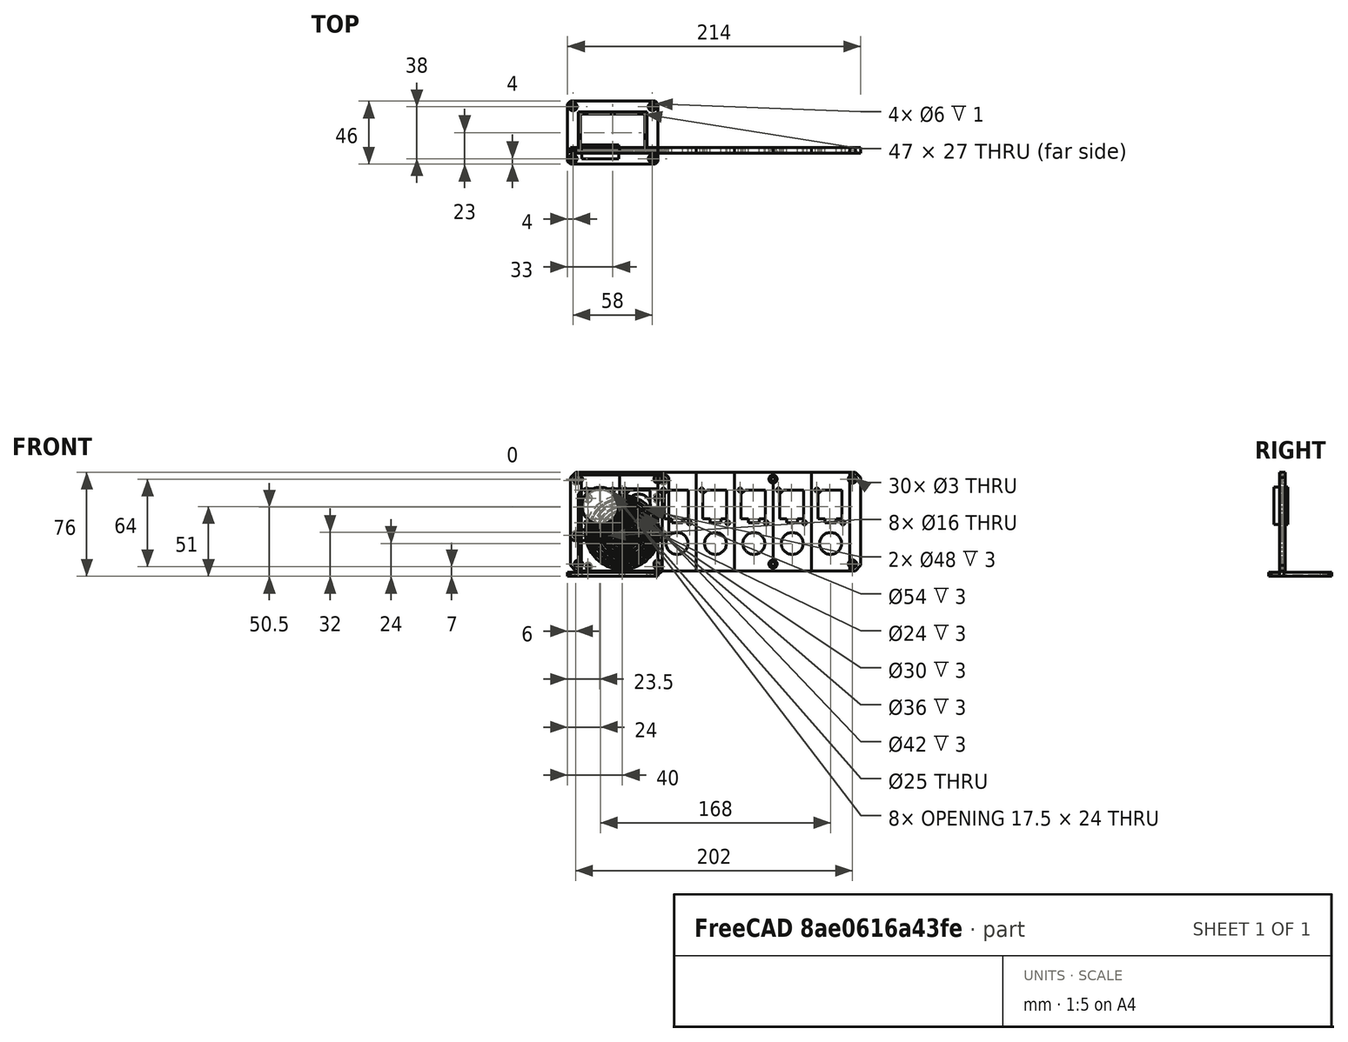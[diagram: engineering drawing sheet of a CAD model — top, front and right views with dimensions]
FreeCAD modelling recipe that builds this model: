
FCSTD DOCUMENT  (FreeCAD 0.19R24276 (Git))
Label: gewisska_016
License: All rights reserved
LicenseURL: http://en.wikipedia.org/wiki/All_rights_reserved
objects: Part::Cylinder×72, Part::Box×36, Part::Compound×34, Part::Cut×26, Part::Chamfer×16, Part::FeaturePython×9, Mesh::Feature×4
note: 193 computed .brp shape members not serialized (recipe doc carries the construction recipe); baked Part::Feature solids carry a one-line shape summary decoded from their .brp

FEATURE [Part::Box] Box  label="Krychle"
  AttacherType = Attacher::AttachEngine3D
  Height = 3
  Length = 50
  Placement = pos=(0,0,0.8) rot=(0,0,1;0rad)
  Width = 30
FEATURE [Part::Box] Box001  label="Krychle001"
  AttacherType = Attacher::AttachEngine3D
  Height = 3
  Length = 66
  Placement = pos=(-8,-8,0) rot=(0,0,1;0rad)
  Width = 46
FEATURE [Part::Box] Box002  label="Krychle002"
  AttacherType = Attacher::AttachEngine3D
  Height = 6
  Length = 47
  Placement = pos=(1.5,1.5,-1) rot=(0,0,1;0rad)
  Width = 27
FEATURE [Part::Cut] Cut
  Base = -> Box001
  Tool = -> Box002
FEATURE [Part::Cut] Cut001
  Base = -> Cut
  Tool = -> Box
FEATURE [Part::Cylinder] Cylinder  label="Válec"
  Angle = 360
  AttacherType = Attacher::AttachEngine3D
  Height = 10
  Placement = pos=(-4,34,-2) rot=(0,0,1;0rad)
  Radius = 1.5
FEATURE [Part::Cylinder] Cylinder001  label="Válec001"
  Angle = 360
  AttacherType = Attacher::AttachEngine3D
  Height = 10
  Placement = pos=(54,-4,-2) rot=(0,0,1;0rad)
  Radius = 1.5
FEATURE [Part::Cylinder] Cylinder002  label="Válec002"
  Angle = 360
  AttacherType = Attacher::AttachEngine3D
  Height = 10
  Placement = pos=(54,34,-2) rot=(0,0,1;0rad)
  Radius = 1.5
FEATURE [Part::Cylinder] Cylinder003  label="Válec003"
  Angle = 360
  AttacherType = Attacher::AttachEngine3D
  Height = 10
  Placement = pos=(-4,-4,-2) rot=(0,0,1;0rad)
  Radius = 1.5
FEATURE [Part::Compound] Compound
  Links = -> [Cylinder,Cylinder001,Cylinder002,Cylinder003]
FEATURE [Part::Cylinder] Cylinder004  label="Válec004"
  Angle = 360
  AttacherType = Attacher::AttachEngine3D
  Height = 3
  Placement = pos=(-4,-4,-2) rot=(0,0,1;0rad)
  Radius = 3
FEATURE [Part::Cylinder] Cylinder005  label="Válec005"
  Angle = 360
  AttacherType = Attacher::AttachEngine3D
  Height = 3
  Placement = pos=(-4,34,-2) rot=(0,0,1;0rad)
  Radius = 3
FEATURE [Part::Cylinder] Cylinder006  label="Válec006"
  Angle = 360
  AttacherType = Attacher::AttachEngine3D
  Height = 3
  Placement = pos=(54,34,-2) rot=(0,0,1;0rad)
  Radius = 3
FEATURE [Part::Cylinder] Cylinder007  label="Válec007"
  Angle = 360
  AttacherType = Attacher::AttachEngine3D
  Height = 3
  Placement = pos=(54,-4,-2) rot=(0,0,1;0rad)
  Radius = 3
FEATURE [Part::Compound] Compound001
  Links = -> [Cylinder005,Cylinder007,Cylinder006,Cylinder004]
  Placement = pos=(0,0,4) rot=(0,0,1;0rad)
FEATURE [Part::Cut] Cut002
  Base = -> Cut001
  Tool = -> Compound
FEATURE [Part::Cut] Cut003
  Base = -> Cut002
  Tool = -> Compound001
FEATURE [Part::Chamfer] Chamfer
  Base = -> Cut003
  Edges = 2 edges r=2: [Edge1,Edge6]
FEATURE [Part::Chamfer] Chamfer001  label="220_zasuvka_drzho"
  Base = -> Chamfer
  Edges = 2 edges r=2: [Edge4,Edge21]
FEATURE [Mesh::Feature] Mesh  label="220_zasuvka_drzho (Meshed)"
FEATURE [Part::Cylinder] Cylinder816  label="Válec816"
  Angle = 360
  AttacherType = Attacher::AttachEngine3D
  Height = 10
  Placement = pos=(29,6,39) rot=(1,0,0;1.5708rad)
  Radius = 1.5
FEATURE [Part::Cylinder] Cylinder815  label="Válec815"
  Angle = 360
  AttacherType = Attacher::AttachEngine3D
  Height = 10
  Placement = pos=(10,6,63) rot=(1,0,0;1.5708rad)
  Radius = 1.5
FEATURE [Part::Compound] Compound477
  Links = -> [Cylinder815,Cylinder816]
  Placement = pos=(-4,0,0) rot=(0,0,1;0rad)
FEATURE [Part::Box] Box390  label="Krychle390"
  AttacherType = Attacher::AttachEngine3D
  Height = 21
  Length = 17.5
  Placement = pos=(10.75,-2,42) rot=(0,0,1;0rad)
  Width = 10
FEATURE [Part::Chamfer] Chamfer014
  Base = -> Box390
  Edges = 1 edges r=3: [Edge2]
  Placement = pos=(-4,0,0) rot=(0,0,1;0rad)
FEATURE [Part::Cylinder] Cylinder828  label="Válec828"
  Angle = 360
  AttacherType = Attacher::AttachEngine3D
  Height = 10
  Placement = pos=(16,6,24) rot=(1,0,0;1.5708rad)
  Radius = 8
FEATURE [Part::Box] Box396  label="Krychle396"
  AttacherType = Attacher::AttachEngine3D
  Height = 3
  Length = 8
  Placement = pos=(12,-2,39) rot=(0,0,1;0rad)
  Width = 10
FEATURE [Part::Compound] Compound478
  Links = -> [Compound477,Chamfer014,Cylinder828,Box396]
FEATURE [Part::Box] Box397  label="Krychle397"
  AttacherType = Attacher::AttachEngine3D
  Height = 72
  Length = 28
  Placement = pos=(2,0,4) rot=(0,0,1;0rad)
  Width = 4
FEATURE [Part::Cut] Cut004
  Base = -> Box397
  Tool = -> Compound478
FEATURE [Part::Box] Box398  label="Krychle398"
  AttacherType = Attacher::AttachEngine3D
  Height = 72
  Length = 28
  Placement = pos=(2,0,4) rot=(0,0,1;0rad)
  Width = 4
FEATURE [Part::Box] Box399  label="Krychle399"
  AttacherType = Attacher::AttachEngine3D
  Height = 21
  Length = 17.5
  Placement = pos=(10.75,-2,42) rot=(0,0,1;0rad)
  Width = 10
FEATURE [Part::Cylinder] Cylinder829  label="Válec829"
  Angle = 360
  AttacherType = Attacher::AttachEngine3D
  Height = 10
  Placement = pos=(16,6,24) rot=(1,0,0;1.5708rad)
  Radius = 8
FEATURE [Part::Cylinder] Cylinder830  label="Válec830"
  Angle = 360
  AttacherType = Attacher::AttachEngine3D
  Height = 10
  Placement = pos=(29,6,39) rot=(1,0,0;1.5708rad)
  Radius = 1.5
FEATURE [Part::Cylinder] Cylinder831  label="Válec831"
  Angle = 360
  AttacherType = Attacher::AttachEngine3D
  Height = 10
  Placement = pos=(10,6,63) rot=(1,0,0;1.5708rad)
  Radius = 1.5
FEATURE [Part::Box] Box400  label="Krychle400"
  AttacherType = Attacher::AttachEngine3D
  Height = 3
  Length = 8
  Placement = pos=(12,-2,39) rot=(0,0,1;0rad)
  Width = 10
FEATURE [Part::Chamfer] Chamfer015
  Base = -> Box399
  Edges = 1 edges r=3: [Edge2]
  Placement = pos=(-4,0,0) rot=(0,0,1;0rad)
FEATURE [Part::Compound] Compound480
  Links = -> [Cylinder831,Cylinder830]
  Placement = pos=(-4,0,0) rot=(0,0,1;0rad)
FEATURE [Part::Compound] Compound479
  Links = -> [Compound480,Chamfer015,Cylinder829,Box400]
FEATURE [Part::Cut] Cut005
  Base = -> Box398
  Placement = pos=(28,0,0) rot=(0,0,1;0rad)
  Tool = -> Compound479
FEATURE [Part::Box] Box401  label="Krychle401"
  AttacherType = Attacher::AttachEngine3D
  Height = 72
  Length = 28
  Placement = pos=(2,0,4) rot=(0,0,1;0rad)
  Width = 4
FEATURE [Part::Box] Box402  label="Krychle402"
  AttacherType = Attacher::AttachEngine3D
  Height = 21
  Length = 17.5
  Placement = pos=(10.75,-2,42) rot=(0,0,1;0rad)
  Width = 10
FEATURE [Part::Cylinder] Cylinder832  label="Válec832"
  Angle = 360
  AttacherType = Attacher::AttachEngine3D
  Height = 10
  Placement = pos=(16,6,24) rot=(1,0,0;1.5708rad)
  Radius = 8
FEATURE [Part::Cylinder] Cylinder833  label="Válec833"
  Angle = 360
  AttacherType = Attacher::AttachEngine3D
  Height = 10
  Placement = pos=(29,6,39) rot=(1,0,0;1.5708rad)
  Radius = 1.5
FEATURE [Part::Cylinder] Cylinder834  label="Válec834"
  Angle = 360
  AttacherType = Attacher::AttachEngine3D
  Height = 10
  Placement = pos=(10,6,63) rot=(1,0,0;1.5708rad)
  Radius = 1.5
FEATURE [Part::Box] Box403  label="Krychle403"
  AttacherType = Attacher::AttachEngine3D
  Height = 3
  Length = 8
  Placement = pos=(12,-2,39) rot=(0,0,1;0rad)
  Width = 10
FEATURE [Part::Chamfer] Chamfer016
  Base = -> Box402
  Edges = 1 edges r=3: [Edge2]
  Placement = pos=(-4,0,0) rot=(0,0,1;0rad)
FEATURE [Part::Compound] Compound482
  Links = -> [Cylinder834,Cylinder833]
  Placement = pos=(-4,0,0) rot=(0,0,1;0rad)
FEATURE [Part::Compound] Compound481
  Links = -> [Compound482,Chamfer016,Cylinder832,Box403]
FEATURE [Part::Cut] Cut006
  Base = -> Box401
  Placement = pos=(56,0,0) rot=(0,0,1;0rad)
  Tool = -> Compound481
FEATURE [Part::Box] Box404  label="Krychle404"
  AttacherType = Attacher::AttachEngine3D
  Height = 72
  Length = 28
  Placement = pos=(2,0,4) rot=(0,0,1;0rad)
  Width = 4
FEATURE [Part::Box] Box405  label="Krychle405"
  AttacherType = Attacher::AttachEngine3D
  Height = 21
  Length = 17.5
  Placement = pos=(10.75,-2,42) rot=(0,0,1;0rad)
  Width = 10
FEATURE [Part::Cylinder] Cylinder835  label="Válec835"
  Angle = 360
  AttacherType = Attacher::AttachEngine3D
  Height = 10
  Placement = pos=(16,6,24) rot=(1,0,0;1.5708rad)
  Radius = 8
FEATURE [Part::Cylinder] Cylinder836  label="Válec836"
  Angle = 360
  AttacherType = Attacher::AttachEngine3D
  Height = 10
  Placement = pos=(29,6,39) rot=(1,0,0;1.5708rad)
  Radius = 1.5
FEATURE [Part::Cylinder] Cylinder837  label="Válec837"
  Angle = 360
  AttacherType = Attacher::AttachEngine3D
  Height = 10
  Placement = pos=(10,6,63) rot=(1,0,0;1.5708rad)
  Radius = 1.5
FEATURE [Part::Box] Box406  label="Krychle406"
  AttacherType = Attacher::AttachEngine3D
  Height = 3
  Length = 8
  Placement = pos=(12,-2,39) rot=(0,0,1;0rad)
  Width = 10
FEATURE [Part::Chamfer] Chamfer017
  Base = -> Box405
  Edges = 1 edges r=3: [Edge2]
  Placement = pos=(-4,0,0) rot=(0,0,1;0rad)
FEATURE [Part::Compound] Compound484
  Links = -> [Cylinder837,Cylinder836]
  Placement = pos=(-4,0,0) rot=(0,0,1;0rad)
FEATURE [Part::Compound] Compound483
  Links = -> [Compound484,Chamfer017,Cylinder835,Box406]
FEATURE [Part::Cut] Cut007
  Base = -> Box404
  Placement = pos=(84,0,0) rot=(0,0,1;0rad)
  Tool = -> Compound483
FEATURE [Part::Box] Box407  label="Krychle407"
  AttacherType = Attacher::AttachEngine3D
  Height = 3
  Length = 8
  Placement = pos=(12,-2,39) rot=(0,0,1;0rad)
  Width = 10
FEATURE [Part::Cylinder] Cylinder838  label="Válec838"
  Angle = 360
  AttacherType = Attacher::AttachEngine3D
  Height = 10
  Placement = pos=(10,6,63) rot=(1,0,0;1.5708rad)
  Radius = 1.5
FEATURE [Part::Cylinder] Cylinder839  label="Válec839"
  Angle = 360
  AttacherType = Attacher::AttachEngine3D
  Height = 10
  Placement = pos=(16,6,24) rot=(1,0,0;1.5708rad)
  Radius = 8
FEATURE [Part::Box] Box408  label="Krychle408"
  AttacherType = Attacher::AttachEngine3D
  Height = 21
  Length = 17.5
  Placement = pos=(10.75,-2,42) rot=(0,0,1;0rad)
  Width = 10
FEATURE [Part::Chamfer] Chamfer018
  Base = -> Box408
  Edges = 1 edges r=3: [Edge2]
  Placement = pos=(-4,0,0) rot=(0,0,1;0rad)
FEATURE [Part::Box] Box409  label="Krychle409"
  AttacherType = Attacher::AttachEngine3D
  Height = 72
  Length = 28
  Placement = pos=(2,0,4) rot=(0,0,1;0rad)
  Width = 4
FEATURE [Part::Cylinder] Cylinder840  label="Válec840"
  Angle = 360
  AttacherType = Attacher::AttachEngine3D
  Height = 10
  Placement = pos=(29,6,39) rot=(1,0,0;1.5708rad)
  Radius = 1.5
FEATURE [Part::Compound] Compound485
  Links = -> [Cylinder838,Cylinder840]
  Placement = pos=(-4,0,0) rot=(0,0,1;0rad)
FEATURE [Part::Compound] Compound486
  Links = -> [Compound485,Chamfer018,Cylinder839,Box407]
FEATURE [Part::Cut] Cut008
  Base = -> Box409
  Placement = pos=(112,0,0) rot=(0,0,1;0rad)
  Tool = -> Compound486
FEATURE [Part::Cylinder] Cylinder841  label="Válec841"
  Angle = 360
  AttacherType = Attacher::AttachEngine3D
  Height = 10
  Placement = pos=(10,6,63) rot=(1,0,0;1.5708rad)
  Radius = 1.5
FEATURE [Part::Box] Box410  label="Krychle410"
  AttacherType = Attacher::AttachEngine3D
  Height = 3
  Length = 8
  Placement = pos=(12,-2,39) rot=(0,0,1;0rad)
  Width = 10
FEATURE [Part::Cylinder] Cylinder842  label="Válec842"
  Angle = 360
  AttacherType = Attacher::AttachEngine3D
  Height = 10
  Placement = pos=(16,6,24) rot=(1,0,0;1.5708rad)
  Radius = 8
FEATURE [Part::Box] Box411  label="Krychle411"
  AttacherType = Attacher::AttachEngine3D
  Height = 21
  Length = 17.5
  Placement = pos=(10.75,-2,42) rot=(0,0,1;0rad)
  Width = 10
FEATURE [Part::Chamfer] Chamfer019
  Base = -> Box411
  Edges = 1 edges r=3: [Edge2]
  Placement = pos=(-4,0,0) rot=(0,0,1;0rad)
FEATURE [Part::Cylinder] Cylinder843  label="Válec843"
  Angle = 360
  AttacherType = Attacher::AttachEngine3D
  Height = 10
  Placement = pos=(29,6,39) rot=(1,0,0;1.5708rad)
  Radius = 1.5
FEATURE [Part::Compound] Compound487
  Links = -> [Cylinder841,Cylinder843]
  Placement = pos=(-4,0,0) rot=(0,0,1;0rad)
FEATURE [Part::Compound] Compound488
  Links = -> [Compound487,Chamfer019,Cylinder842,Box410]
FEATURE [Part::Box] Box412  label="Krychle412"
  AttacherType = Attacher::AttachEngine3D
  Height = 72
  Length = 28
  Placement = pos=(2,0,4) rot=(0,0,1;0rad)
  Width = 4
FEATURE [Part::Cut] Cut009
  Base = -> Box412
  Placement = pos=(140,0,0) rot=(0,0,1;0rad)
  Tool = -> Compound488
FEATURE [Part::Cylinder] Cylinder844  label="Válec844"
  Angle = 360
  AttacherType = Attacher::AttachEngine3D
  Height = 10
  Placement = pos=(10,6,63) rot=(1,0,0;1.5708rad)
  Radius = 1.5
FEATURE [Part::Box] Box413  label="Krychle413"
  AttacherType = Attacher::AttachEngine3D
  Height = 3
  Length = 8
  Placement = pos=(12,-2,39) rot=(0,0,1;0rad)
  Width = 10
FEATURE [Part::Cylinder] Cylinder845  label="Válec845"
  Angle = 360
  AttacherType = Attacher::AttachEngine3D
  Height = 10
  Placement = pos=(16,6,24) rot=(1,0,0;1.5708rad)
  Radius = 8
FEATURE [Part::Box] Box414  label="Krychle414"
  AttacherType = Attacher::AttachEngine3D
  Height = 21
  Length = 17.5
  Placement = pos=(10.75,-2,42) rot=(0,0,1;0rad)
  Width = 10
FEATURE [Part::Chamfer] Chamfer020
  Base = -> Box414
  Edges = 1 edges r=3: [Edge2]
  Placement = pos=(-4,0,0) rot=(0,0,1;0rad)
FEATURE [Part::Cylinder] Cylinder846  label="Válec846"
  Angle = 360
  AttacherType = Attacher::AttachEngine3D
  Height = 10
  Placement = pos=(29,6,39) rot=(1,0,0;1.5708rad)
  Radius = 1.5
FEATURE [Part::Compound] Compound489
  Links = -> [Cylinder844,Cylinder846]
  Placement = pos=(-4,0,0) rot=(0,0,1;0rad)
FEATURE [Part::Compound] Compound490
  Links = -> [Compound489,Chamfer020,Cylinder845,Box413]
FEATURE [Part::Box] Box415  label="Krychle415"
  AttacherType = Attacher::AttachEngine3D
  Height = 72
  Length = 28
  Placement = pos=(2,0,4) rot=(0,0,1;0rad)
  Width = 4
FEATURE [Part::Cut] Cut010
  Base = -> Box415
  Placement = pos=(168,0,0) rot=(0,0,1;0rad)
  Tool = -> Compound490
FEATURE [Part::Compound] Compound491
  Links = -> [Cut004,Cut005,Cut008,Cut009,Cut010,Cut007,Cut006]
FEATURE [Part::Box] Box416  label="Krychle416"
  AttacherType = Attacher::AttachEngine3D
  Height = 72
  Length = 8
  Placement = pos=(-6,0,4) rot=(0,0,1;0rad)
  Width = 4
FEATURE [Part::Box] Box417  label="Krychle417"
  AttacherType = Attacher::AttachEngine3D
  Height = 72
  Length = 8
  Placement = pos=(198,0,4) rot=(0,0,1;0rad)
  Width = 4
FEATURE [Part::Cylinder] Cylinder847  label="Válec847"
  Angle = 360
  AttacherType = Attacher::AttachEngine3D
  Height = 10
  Placement = pos=(0,4,13) rot=(1,0,0;1.5708rad)
  Radius = 1.5
FEATURE [Part::Cylinder] Cylinder848  label="Válec848"
  Angle = 360
  AttacherType = Attacher::AttachEngine3D
  Height = 10
  Placement = pos=(58,4,13) rot=(1,0,0;1.5708rad)
  Radius = 1.5
FEATURE [Part::Cylinder] Cylinder849  label="Válec849"
  Angle = 360
  AttacherType = Attacher::AttachEngine3D
  Height = 10
  Placement = pos=(200,4,13) rot=(1,0,0;1.5708rad)
  Radius = 1.5
FEATURE [Part::Cylinder] Cylinder850  label="Válec850"
  Angle = 360
  AttacherType = Attacher::AttachEngine3D
  Height = 10
  Placement = pos=(142,4,13) rot=(1,0,0;1.5708rad)
  Radius = 1.5
FEATURE [Part::Compound] Compound492
  Links = -> [Cylinder847,Cylinder848,Cylinder849,Cylinder850]
  Placement = pos=(0,0,-4) rot=(0,0,1;0rad)
FEATURE [Part::Cylinder] Cylinder851  label="Válec851"
  Angle = 360
  AttacherType = Attacher::AttachEngine3D
  Height = 3
  Placement = pos=(142,4,13) rot=(1,0,0;1.5708rad)
  Radius = 3
FEATURE [Part::Cylinder] Cylinder852  label="Válec852"
  Angle = 360
  AttacherType = Attacher::AttachEngine3D
  Height = 3
  Placement = pos=(0,4,13) rot=(1,0,0;1.5708rad)
  Radius = 3
FEATURE [Part::Cylinder] Cylinder853  label="Válec853"
  Angle = 360
  AttacherType = Attacher::AttachEngine3D
  Height = 3
  Placement = pos=(200,4,13) rot=(1,0,0;1.5708rad)
  Radius = 3
FEATURE [Part::Cylinder] Cylinder854  label="Válec854"
  Angle = 360
  AttacherType = Attacher::AttachEngine3D
  Height = 3
  Placement = pos=(58,4,13) rot=(1,0,0;1.5708rad)
  Radius = 3
FEATURE [Part::Compound] Compound493
  Links = -> [Cylinder852,Cylinder854,Cylinder853,Cylinder851]
  Placement = pos=(0,-2,58) rot=(0,0,1;0rad)
FEATURE [Part::Cylinder] Cylinder855  label="Válec855"
  Angle = 360
  AttacherType = Attacher::AttachEngine3D
  Height = 10
  Placement = pos=(0,4,13) rot=(1,0,0;1.5708rad)
  Radius = 1.5
FEATURE [Part::Cylinder] Cylinder856  label="Válec856"
  Angle = 360
  AttacherType = Attacher::AttachEngine3D
  Height = 10
  Placement = pos=(58,4,13) rot=(1,0,0;1.5708rad)
  Radius = 1.5
FEATURE [Part::Cylinder] Cylinder857  label="Válec857"
  Angle = 360
  AttacherType = Attacher::AttachEngine3D
  Height = 10
  Placement = pos=(142,4,13) rot=(1,0,0;1.5708rad)
  Radius = 1.5
FEATURE [Part::Cylinder] Cylinder858  label="Válec858"
  Angle = 360
  AttacherType = Attacher::AttachEngine3D
  Height = 3
  Placement = pos=(142,4,13) rot=(1,0,0;1.5708rad)
  Radius = 3
FEATURE [Part::Cylinder] Cylinder859  label="Válec859"
  Angle = 360
  AttacherType = Attacher::AttachEngine3D
  Height = 3
  Placement = pos=(0,4,13) rot=(1,0,0;1.5708rad)
  Radius = 3
FEATURE [Part::Cylinder] Cylinder860  label="Válec860"
  Angle = 360
  AttacherType = Attacher::AttachEngine3D
  Height = 3
  Placement = pos=(200,4,13) rot=(1,0,0;1.5708rad)
  Radius = 3
FEATURE [Part::Cylinder] Cylinder861  label="Válec861"
  Angle = 360
  AttacherType = Attacher::AttachEngine3D
  Height = 3
  Placement = pos=(58,4,13) rot=(1,0,0;1.5708rad)
  Radius = 3
FEATURE [Part::Cylinder] Cylinder862  label="Válec862"
  Angle = 360
  AttacherType = Attacher::AttachEngine3D
  Height = 10
  Placement = pos=(200,4,13) rot=(1,0,0;1.5708rad)
  Radius = 1.5
FEATURE [Part::Compound] Compound494
  Links = -> [Cylinder855,Cylinder856,Cylinder862,Cylinder857]
  Placement = pos=(0,0,58) rot=(0,0,1;0rad)
FEATURE [Part::Compound] Compound495
  Links = -> [Cylinder859,Cylinder861,Cylinder860,Cylinder858]
  Placement = pos=(0,-2,-4) rot=(0,0,1;0rad)
FEATURE [Part::Compound] Compound496
  Links = -> [Box416,Box417]
FEATURE [Part::Compound] Compound497
  Links = -> [Compound496,Compound491]
FEATURE [Part::Cut] Cut011
  Base = -> Compound497
  Tool = -> Compound492
FEATURE [Part::Cut] Cut012
  Base = -> Cut011
  Tool = -> Compound494
FEATURE [Part::Cut] Cut013
  Base = -> Cut012
  Tool = -> Compound495
FEATURE [Part::Cut] Cut014
  Base = -> Cut013
  Tool = -> Compound493
FEATURE [Part::Chamfer] Chamfer021
  Base = -> Cut014
  Edges = 2 edges r=4: [Edge2,Edge4]
FEATURE [Part::Chamfer] Chamfer022  label="zasuvkovy_panel"
  Base = -> Chamfer021
  Edges = 2 edges r=4: [Edge65,Edge70]
FEATURE [Mesh::Feature] Mesh001  label="zasuvkovy_panel (Meshed)"
FEATURE [Part::Box] Box418  label="Krychle418"
  AttacherType = Attacher::AttachEngine3D
  Height = 64
  Length = 61
  Width = 3
FEATURE [Part::Cylinder] Cylinder863  label="Válec863"
  Angle = 360
  AttacherType = Attacher::AttachEngine3D
  Height = 10
  Placement = pos=(0,0,0) rot=(1,0,0;1.5708rad)
  Radius = 1.5
FEATURE [Part::Cylinder] Cylinder864  label="Válec864"
  Angle = 360
  AttacherType = Attacher::AttachEngine3D
  Height = 10
  Placement = pos=(50,0,0) rot=(1,0,0;1.5708rad)
  Radius = 1.5
FEATURE [Part::Cylinder] Cylinder865  label="Válec865"
  Angle = 360
  AttacherType = Attacher::AttachEngine3D
  Height = 10
  Placement = pos=(50,0,50) rot=(1,0,0;1.5708rad)
  Radius = 1.5
FEATURE [Part::Cylinder] Cylinder866  label="Válec866"
  Angle = 360
  AttacherType = Attacher::AttachEngine3D
  Height = 10
  Placement = pos=(0,0,50) rot=(1,0,0;1.5708rad)
  Radius = 1.5
FEATURE [Part::Compound] Compound498
  Links = -> [Cylinder863,Cylinder864,Cylinder865,Cylinder866]
  Placement = pos=(7,4,7) rot=(0,0,1;0rad)
FEATURE [Part::Cut] Cut015
  Base = -> Box418
  Tool = -> Compound498
FEATURE [Part::Cylinder] Cylinder867  label="Válec867"
  Angle = 360
  AttacherType = Attacher::AttachEngine3D
  Height = 10
  Placement = pos=(32,5,32) rot=(1,0,0;1.5708rad)
  Radius = 27
FEATURE [Part::Cut] Cut016
  Base = -> Cut015
  Tool = -> Cylinder867
FEATURE [Part::FeaturePython] Tube  # WARN: FeaturePython — macro-defined, semantics opaque (R4)
  AttacherType = Attacher::AttachEngine3D
  Height = 3
  InnerRadius = 3
  OuterRadius = 4
  Placement = pos=(32,3,32) rot=(1,0,0;1.5708rad)
FEATURE [Part::FeaturePython] Tube001  # WARN: FeaturePython — macro-defined, semantics opaque (R4)
  AttacherType = Attacher::AttachEngine3D
  Height = 3
  InnerRadius = 6
  OuterRadius = 7
  Placement = pos=(32,3,32) rot=(1,0,0;1.5708rad)
FEATURE [Part::FeaturePython] Tube002  # WARN: FeaturePython — macro-defined, semantics opaque (R4)
  AttacherType = Attacher::AttachEngine3D
  Height = 3
  InnerRadius = 9
  OuterRadius = 10
  Placement = pos=(32,3,32) rot=(1,0,0;1.5708rad)
FEATURE [Part::FeaturePython] Tube003  # WARN: FeaturePython — macro-defined, semantics opaque (R4)
  AttacherType = Attacher::AttachEngine3D
  Height = 3
  InnerRadius = 12
  OuterRadius = 13
  Placement = pos=(32,3,32) rot=(1,0,0;1.5708rad)
FEATURE [Part::FeaturePython] Tube004  # WARN: FeaturePython — macro-defined, semantics opaque (R4)
  AttacherType = Attacher::AttachEngine3D
  Height = 3
  InnerRadius = 15
  OuterRadius = 16
  Placement = pos=(32,3,32) rot=(1,0,0;1.5708rad)
FEATURE [Part::FeaturePython] Tube005  # WARN: FeaturePython — macro-defined, semantics opaque (R4)
  AttacherType = Attacher::AttachEngine3D
  Height = 3
  InnerRadius = 18
  OuterRadius = 19
  Placement = pos=(32,3,32) rot=(1,0,0;1.5708rad)
FEATURE [Part::FeaturePython] Tube006  # WARN: FeaturePython — macro-defined, semantics opaque (R4)
  AttacherType = Attacher::AttachEngine3D
  Height = 3
  InnerRadius = 21
  OuterRadius = 22
  Placement = pos=(32,3,32) rot=(1,0,0;1.5708rad)
FEATURE [Part::FeaturePython] Tube007  # WARN: FeaturePython — macro-defined, semantics opaque (R4)
  AttacherType = Attacher::AttachEngine3D
  Height = 3
  InnerRadius = 24
  OuterRadius = 25
  Placement = pos=(32,3,32) rot=(1,0,0;1.5708rad)
FEATURE [Part::FeaturePython] Tube008  # WARN: FeaturePython — macro-defined, semantics opaque (R4)
  AttacherType = Attacher::AttachEngine3D
  Height = 3
  InnerRadius = 24
  OuterRadius = 25
  Placement = pos=(32,3,32) rot=(1,0,0;1.5708rad)
FEATURE [Part::Box] Box419  label="Krychle419"
  AttacherType = Attacher::AttachEngine3D
  Height = 64
  Length = 4
  Placement = pos=(30,0,0) rot=(0,0,1;0rad)
  Width = 3
FEATURE [Part::Box] Box420  label="Krychle420"
  AttacherType = Attacher::AttachEngine3D
  Height = 4
  Length = 61
  Placement = pos=(0,0,30) rot=(0,0,1;0rad)
  Width = 3
FEATURE [Part::Cylinder] Cylinder868  label="Válec868"
  Angle = 360
  AttacherType = Attacher::AttachEngine3D
  Height = 10
  Placement = pos=(32,5,32) rot=(1,0,0;1.5708rad)
  Radius = 3
FEATURE [Part::Cylinder] Cylinder869  label="Válec869"
  Angle = 360
  AttacherType = Attacher::AttachEngine3D
  Height = 10
  Placement = pos=(32,5,32) rot=(1,0,0;1.5708rad)
  Radius = 3
FEATURE [Part::Cut] Cut017
  Base = -> Box419
  Tool = -> Cylinder868
FEATURE [Part::Cut] Cut018
  Base = -> Box420
  Tool = -> Cylinder869
FEATURE [Part::Cylinder] Cylinder870  label="Válec870"
  Angle = 360
  AttacherType = Attacher::AttachEngine3D
  Height = 3
  Placement = pos=(0,0,0) rot=(1,0,0;1.5708rad)
  Radius = 3
FEATURE [Part::Cylinder] Cylinder871  label="Válec871"
  Angle = 360
  AttacherType = Attacher::AttachEngine3D
  Height = 3
  Placement = pos=(50,0,0) rot=(1,0,0;1.5708rad)
  Radius = 3
FEATURE [Part::Cylinder] Cylinder872  label="Válec872"
  Angle = 360
  AttacherType = Attacher::AttachEngine3D
  Height = 3
  Placement = pos=(50,0,50) rot=(1,0,0;1.5708rad)
  Radius = 3
FEATURE [Part::Cylinder] Cylinder873  label="Válec873"
  Angle = 360
  AttacherType = Attacher::AttachEngine3D
  Height = 3
  Placement = pos=(0,0,50) rot=(1,0,0;1.5708rad)
  Radius = 3
FEATURE [Part::Compound] Compound499
  Links = -> [Cylinder870,Cylinder871,Cylinder872,Cylinder873]
  Placement = pos=(7,5,7) rot=(0,0,1;0rad)
FEATURE [Part::Cut] Cut019
  Base = -> Cut016
  Tool = -> Compound499
FEATURE [Part::Chamfer] Chamfer023
  Base = -> Cut019
  Edges = 2 edges r=4: [Edge4,Edge22]
FEATURE [Part::Chamfer] Chamfer024
  Base = -> Chamfer023
  Edges = 2 edges r=4: [Edge4,Edge18]
FEATURE [Part::Compound] Compound500
  Links = -> [Tube,Tube001,Tube002,Tube003,Tube004,Tube005,Tube006,Tube007,Tube008]
FEATURE [Part::Compound] Compound501  label="vetrako_kryt"
  Links = -> [Cut017,Cut018,Chamfer024,Compound500]
FEATURE [Mesh::Feature] Mesh002  label="vetrako_kryt (Meshed)"
FEATURE [Part::Cylinder] Cylinder874  label="Válec874"
  Angle = 360
  AttacherType = Attacher::AttachEngine3D
  Height = 10
  Placement = pos=(16,6,24) rot=(1,0,0;1.5708rad)
  Radius = 8
FEATURE [Part::Box] Box421  label="Krychle421"
  AttacherType = Attacher::AttachEngine3D
  Height = 3
  Length = 8
  Placement = pos=(12,-2,39) rot=(0,0,1;0rad)
  Width = 10
FEATURE [Part::Box] Box422  label="Krychle422"
  AttacherType = Attacher::AttachEngine3D
  Height = 72
  Length = 28
  Placement = pos=(2,0,4) rot=(0,0,1;0rad)
  Width = 4
FEATURE [Part::Cylinder] Cylinder875  label="Válec875"
  Angle = 360
  AttacherType = Attacher::AttachEngine3D
  Height = 10
  Placement = pos=(29,6,39) rot=(1,0,0;1.5708rad)
  Radius = 1.5
FEATURE [Part::Cylinder] Cylinder876  label="Válec876"
  Angle = 360
  AttacherType = Attacher::AttachEngine3D
  Height = 10
  Placement = pos=(10,6,63) rot=(1,0,0;1.5708rad)
  Radius = 1.5
FEATURE [Part::Box] Box423  label="Krychle423"
  AttacherType = Attacher::AttachEngine3D
  Height = 21
  Length = 17.5
  Placement = pos=(10.75,-2,42) rot=(0,0,1;0rad)
  Width = 10
FEATURE [Part::Compound] Compound503
  Links = -> [Cylinder876,Cylinder875]
  Placement = pos=(-4,0,0) rot=(0,0,1;0rad)
FEATURE [Part::Chamfer] Chamfer025
  Base = -> Box423
  Edges = 1 edges r=3: [Edge2]
  Placement = pos=(-4,0,0) rot=(0,0,1;0rad)
FEATURE [Part::Compound] Compound502
  Links = -> [Compound503,Chamfer025,Cylinder874,Box421]
FEATURE [Part::Cut] Cut020
  Base = -> Box422
  Tool = -> Compound502
FEATURE [Part::Cylinder] Cylinder877  label="Válec877"
  Angle = 360
  AttacherType = Attacher::AttachEngine3D
  Height = 10
  Placement = pos=(29,6,63) rot=(1,0,0;1.5708rad)
  Radius = 1.5
FEATURE [Part::Cylinder] Cylinder878  label="Válec878"
  Angle = 360
  AttacherType = Attacher::AttachEngine3D
  Height = 10
  Placement = pos=(10,6,39) rot=(1,0,0;1.5708rad)
  Radius = 1.5
FEATURE [Part::Compound] Compound504
  Links = -> [Cylinder878,Cylinder877]
  Placement = pos=(-4,0,0) rot=(0,0,1;0rad)
FEATURE [Part::Box] Box424  label="Krychle424"
  AttacherType = Attacher::AttachEngine3D
  Height = 48
  Length = 28
  Placement = pos=(2,0,26) rot=(0,0,1;0rad)
  Width = 4
FEATURE [Part::Cut] Cut021
  Base = -> Box424
  Tool = -> Compound504
FEATURE [Part::Cylinder] Cylinder879  label="Válec879"
  Angle = 360
  AttacherType = Attacher::AttachEngine3D
  Height = 10
  Placement = pos=(16,7,50.5) rot=(1,0,0;1.5708rad)
  Radius = 12.5
FEATURE [Part::Cylinder] Cylinder880  label="Válec880"
  Angle = 360
  AttacherType = Attacher::AttachEngine3D
  Height = 10
  Placement = pos=(16,6,51.5) rot=(1,0,0;1.5708rad)
  Radius = 13.5
FEATURE [Part::Cut] Cut022
  Base = -> Cut021
  Tool = -> Cylinder879
FEATURE [Part::Box] Box425  label="Krychle425"
  AttacherType = Attacher::AttachEngine3D
  Height = 48
  Length = 28
  Placement = pos=(30,0,26) rot=(0,0,1;0rad)
  Width = 4
FEATURE [Part::Cylinder] Cylinder881  label="Válec881"
  Angle = 360
  AttacherType = Attacher::AttachEngine3D
  Height = 10
  Placement = pos=(44,6,51.5) rot=(1,0,0;1.5708rad)
  Radius = 8.5
FEATURE [Part::Cut] Cut023
  Base = -> Box425
  Tool = -> Cylinder881
FEATURE [Part::Cylinder] Cylinder882  label="Válec882"
  Angle = 360
  AttacherType = Attacher::AttachEngine3D
  Height = 3
  Placement = pos=(-2,4,30) rot=(1,0,0;1.5708rad)
  Radius = 3
FEATURE [Part::Cylinder] Cylinder883  label="Válec883"
  Angle = 360
  AttacherType = Attacher::AttachEngine3D
  Height = 3
  Placement = pos=(-2,4,70) rot=(1,0,0;1.5708rad)
  Radius = 3
FEATURE [Part::Cylinder] Cylinder884  label="Válec884"
  Angle = 360
  AttacherType = Attacher::AttachEngine3D
  Height = 10
  Placement = pos=(-2,4,30) rot=(1,0,0;1.5708rad)
  Radius = 1.5
FEATURE [Part::Cylinder] Cylinder885  label="Válec885"
  Angle = 360
  AttacherType = Attacher::AttachEngine3D
  Height = 10
  Placement = pos=(-2,4,70) rot=(1,0,0;1.5708rad)
  Radius = 1.5
FEATURE [Part::Cylinder] Cylinder886  label="Válec886"
  Angle = 360
  AttacherType = Attacher::AttachEngine3D
  Height = 3
  Placement = pos=(62,4,30) rot=(1,0,0;1.5708rad)
  Radius = 3
FEATURE [Part::Cylinder] Cylinder887  label="Válec887"
  Angle = 360
  AttacherType = Attacher::AttachEngine3D
  Height = 3
  Placement = pos=(62,4,70) rot=(1,0,0;1.5708rad)
  Radius = 3
FEATURE [Part::Cylinder] Cylinder888  label="Válec888"
  Angle = 360
  AttacherType = Attacher::AttachEngine3D
  Height = 10
  Placement = pos=(62,4,30) rot=(1,0,0;1.5708rad)
  Radius = 1.5
FEATURE [Part::Cylinder] Cylinder889  label="Válec889"
  Angle = 360
  AttacherType = Attacher::AttachEngine3D
  Height = 10
  Placement = pos=(62,4,70) rot=(1,0,0;1.5708rad)
  Radius = 1.5
FEATURE [Part::Box] Box426  label="Krychle426"
  AttacherType = Attacher::AttachEngine3D
  Height = 48
  Length = 8
  Placement = pos=(-6,0,26) rot=(0,0,1;0rad)
  Width = 4
FEATURE [Part::Box] Box427  label="Krychle427"
  AttacherType = Attacher::AttachEngine3D
  Height = 48
  Length = 8
  Placement = pos=(58,0,26) rot=(0,0,1;0rad)
  Width = 4
FEATURE [Part::Compound] Compound505
  Links = -> [Box426,Box427]
FEATURE [Part::Compound] Compound506
  Links = -> [Cylinder886,Cylinder887,Cylinder882,Cylinder883]
  Placement = pos=(0,1,0) rot=(0,0,1;0rad)
FEATURE [Part::Compound] Compound507
  Links = -> [Cylinder884,Cylinder885,Cylinder888,Cylinder889]
FEATURE [Part::Cut] Cut024
  Base = -> Compound505
  Tool = -> Compound507
FEATURE [Part::Cut] Cut025
  Base = -> Cut024
  Tool = -> Compound506
FEATURE [Part::Chamfer] Chamfer026
  Base = -> Cut025
  Edges = 2 edges r=2: [Edge35,Edge40]
FEATURE [Part::Chamfer] Chamfer027
  Base = -> Chamfer026
  Edges = 2 edges r=2: [Edge32,Edge34]
FEATURE [Part::Compound] Compound508  label="komuno_panel"
  Links = -> [Chamfer027,Cut023,Cut022]
FEATURE [Mesh::Feature] Mesh003  label="komuno_panel (Meshed)"
